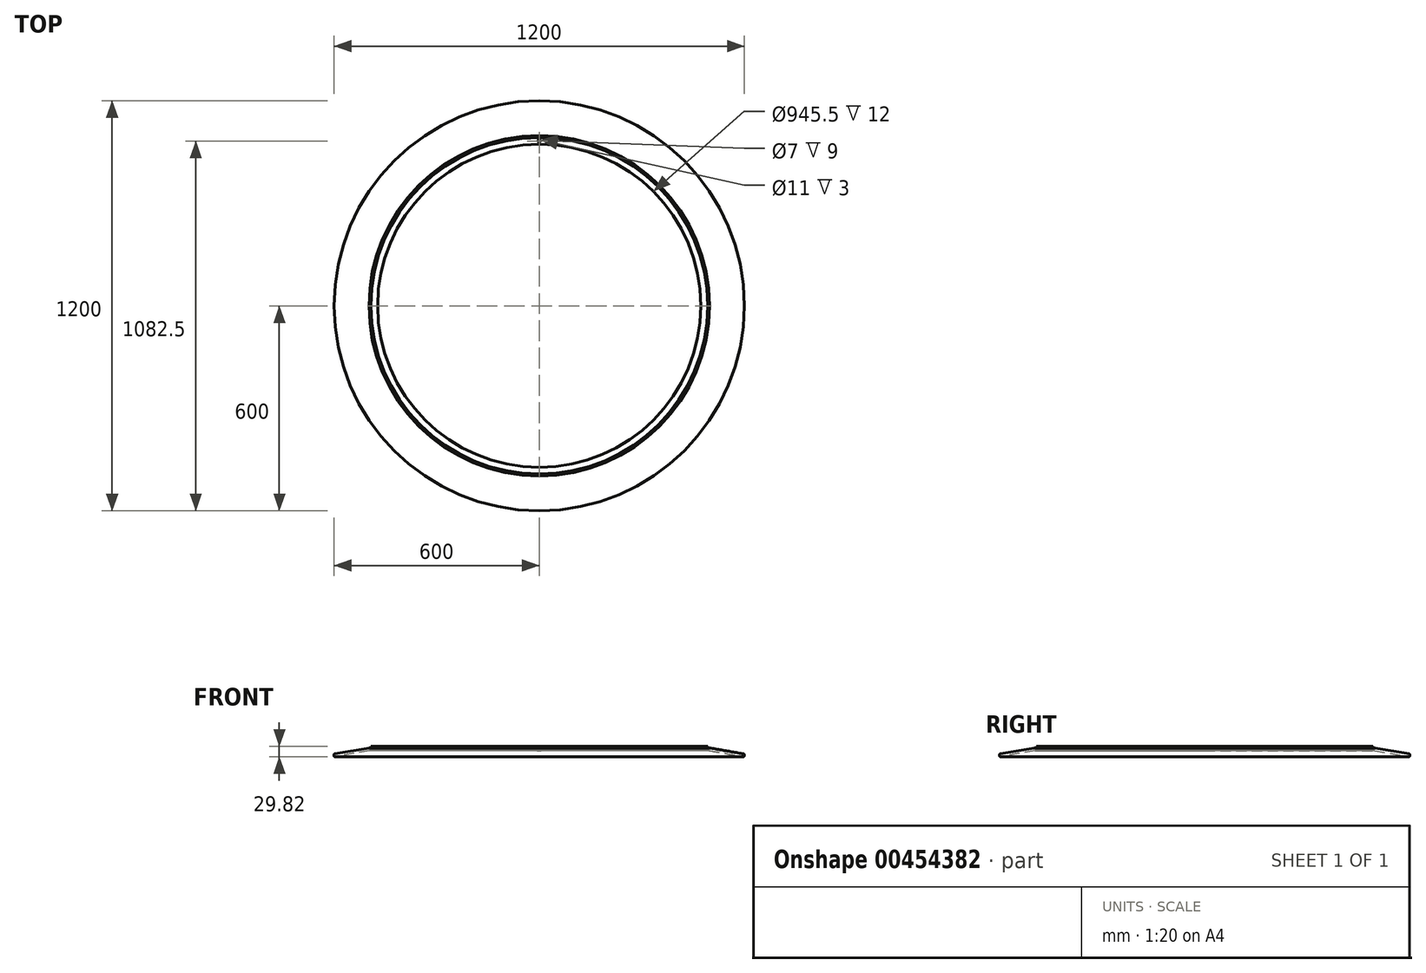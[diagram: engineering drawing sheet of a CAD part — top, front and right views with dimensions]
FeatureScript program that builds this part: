
annotation { "Feature Type Name" : "Feature", "Feature Type Description" : "" }
export const myFeature = defineFeature(function(context is Context, id is Id, definition is map)
    precondition{}
    {
        {
            var Q0;
            Q0=qCreatedBy(makeId("Front.planeOp"),FACE);
            var sketch = newSketch(context, id + "F0", { "sketchPlane" : qUnion([Q0])});
            skLineSegment(sketch, "E0", {"start": v(-472.75, 0) * mm, "end": v(-492.5, 0) * mm});
            skLineSegment(sketch, "E1", {"start": v(0, 0) * mm, "end": v(0, -404.95) * mm});
            skLineSegment(sketch, "E2", {"start": v(-496.78, -12) * mm, "end": v(-472.75, -12) * mm});
            skLineSegment(sketch, "E3", {"start": v(-492.5, 0) * mm, "end": v(-492.5, -4) * mm});
            skLineSegment(sketch, "E4", {"start": v(-597.65, -29.79) * mm, "end": v(-496.78, -12) * mm});
            skLineSegment(sketch, "E5.0", {"start": v(-598.35, -21.79) * mm, "end": v(-498.17, -4.12) * mm});
            skPoint(sketch, "E6.visualSharp", {"position": v(-597.05, -21.56) * mm});
            skPoint(sketch, "E7.visualSharp", {"position": v(-595.66, -29.43) * mm});
            skLineSegment(sketch, "E8.0", {"start": v(-597.7, -25.73) * mm, "end": v(-597.7, -25.73) * mm});
            skLineSegment(sketch, "E9", {"start": v(-498.17, -4.12) * mm, "end": v(-492.5, -4) * mm});
            skLineSegment(sketch, "E10", {"start": v(-472.75, 0) * mm, "end": v(-472.75, -12) * mm});
            skLineSegment(sketch, "E11", {"start": v(-600, -23.75) * mm, "end": v(-600, -27.82) * mm});
            skArc(sketch, "E12.filletArc", {"start": v(-598.35, -21.79) * mm, "mid": v(-599.53, -22.47) * mm, "end": v(-600, -23.75) * mm});
            skArc(sketch, "E13.filletArc", {"start": v(-600, -27.82) * mm, "mid": v(-599.29, -29.35) * mm, "end": v(-597.65, -29.79) * mm});
            skSolve(sketch);
        }
        {
            var Q0;
            Q0=qSketchRegion(id+"F0",true);
            var Q1;
            Q1=sQuery(id+"F0.wireOp",EDGE,"E1");
            revolve(context, id + "F1", {"entities" : qUnion([Q0]), "axis" : qUnion([Q1]), "revolveType" : RevolveType.FULL});
        }
        {
            var Q0;
            Q0=makeQuery(id+"F1.opRevolve","SWEPT_FACE",FACE,{"disambiguationData":[OSD([sQuery(id+"F0.wireOp",EDGE,"E2")])]});
            var sketch = newSketch(context, id + "F2", { "sketchPlane" : qUnion([Q0])});
            skPoint(sketch, "E14", {"position": v(0, -482.5) * mm});
            skSolve(sketch);
        }
        {
            var Q0;
            Q0=sQuery(id+"F2.wireOp",VERTEX,"E14");
            var Q1;
            Q1=makeQuery(id+"F1.opRevolve","SWEPT_BODY",BODY,{"disambiguationData":[OSD([sQuery(id+"F0.wireOp",EDGE,"E0"),sQuery(id+"F0.wireOp",EDGE,"E2"),sQuery(id+"F0.wireOp",EDGE,"E3"),sQuery(id+"F0.wireOp",EDGE,"E4"),sQuery(id+"F0.wireOp",EDGE,"E5.0"),sQuery(id+"F0.wireOp",EDGE,"n0Ym9N2N-7Y1A-0sEX-CREv-p7v7B4GLDR6z"),sQuery(id+"F0.wireOp",EDGE,"pmPgg74l-PZ2B-t6EN-uDR7-zaehnelkuvfk"),sQuery(id+"F0.wireOp",EDGE,"rqI6rkpz-KXuX-LiwP-SoMl-CVp5g7nidQUy"),sQuery(id+"F0.wireOp",EDGE,"E9"),sQuery(id+"F0.wireOp",EDGE,"E10")])]});
            hole(context, id + "F3", {"style" : HoleStyle.C_BORE, "endStyle" : HoleEndStyle.BLIND, "holeDiameter" : 7 * mm, "cBoreDiameter" : 11 * mm, "cBoreDepth" : 3 * mm, "majorDiameter" : 5 * mm, "holeDepth" : 50 * mm, "isTappedThrough" : true, "tappedDepth" : 12 * mm, "tapClearance" : 3, "locations" : qUnion([Q0]), "scope" : qUnion([Q1])});
        }
        {
            var Q0;
            Q0=makeQuery(id+"F1.opRevolve","SWEPT_EDGE",EDGE,{"disambiguationData":[OSD([sQuery(id+"F0.wireOp",EDGE,"E3"),sQuery(id+"F0.wireOp",EDGE,"E9")])]});
            fillet(context, id + "F4", {"entities" : qUnion([Q0]), "radius" : 2 * mm, "tangentPropagation" : true, "allowEdgeOverflow" : false});
        }
    });
